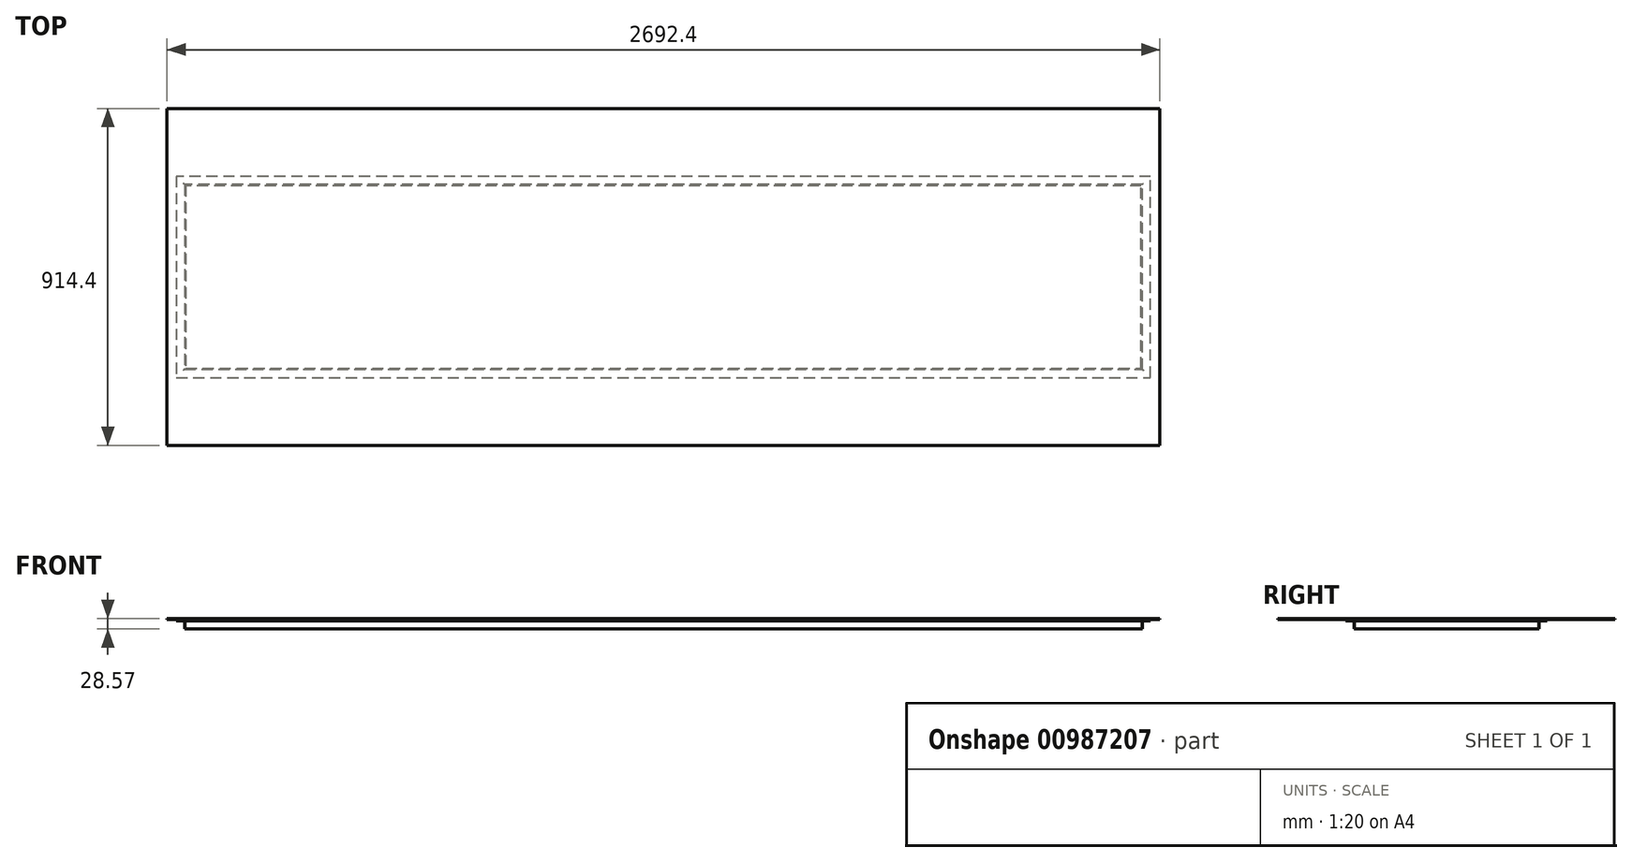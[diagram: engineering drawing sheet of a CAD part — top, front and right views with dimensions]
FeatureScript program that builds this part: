
annotation { "Feature Type Name" : "Feature", "Feature Type Description" : "" }
export const myFeature = defineFeature(function(context is Context, id is Id, definition is map)
    precondition{}
    {
        {
            var Q0;
            Q0=qCreatedBy(makeId("Top.planeOp"),FACE);
            var sketch = newSketch(context, id + "F0", { "sketchPlane" : qUnion([Q0])});
            skLineSegment(sketch, "E0.bottom", {"start": v(-1346.2, 457.2) * mm, "end": v(1346.2, 457.2) * mm});
            skLineSegment(sketch, "E0.top", {"start": v(-1346.2, -457.2) * mm, "end": v(1346.2, -457.2) * mm});
            skLineSegment(sketch, "E0.left", {"start": v(-1346.2, 457.2) * mm, "end": v(-1346.2, -457.2) * mm});
            skLineSegment(sketch, "E0.right", {"start": v(1346.2, 457.2) * mm, "end": v(1346.2, -457.2) * mm});
            skSolve(sketch);
        }
        {
            var Q0;
            Q0=makeQuery(id+"F0.imprint","IMPRINT",FACE,{"disambiguationData":[TD([[makeQuery(id+"F0.imprint","IMPRINT",EDGE,{"derivedFrom":sQuery(id+"F0.wireOp",EDGE,"E0.bottom")}),-1.0]])]});
            extrude(context, id + "F1", {"entities" : qUnion([Q0]), "depth" : 3.17 * mm, "offsetDistance" : 25.4 * mm});
        }
        {
            var Q0;
            Q0=makeQuery(id+"F1.opExtrude","CAP_FACE",FACE,{"disambiguationData":[OSD([sQuery(id+"F0.wireOp",EDGE,"E0.bottom"),sQuery(id+"F0.wireOp",EDGE,"E0.top"),sQuery(id+"F0.wireOp",EDGE,"E0.left"),sQuery(id+"F0.wireOp",EDGE,"E0.right")])],"isStart":true});
            var sketch = newSketch(context, id + "F2", { "sketchPlane" : qUnion([Q0])});
            skLineSegment(sketch, "E1.0", {"start": v(1295.4, 247.65) * mm, "end": v(-1295.4, 247.65) * mm});
            skLineSegment(sketch, "E2.0", {"start": v(-1295.4, 247.65) * mm, "end": v(-1295.4, -247.65) * mm});
            skLineSegment(sketch, "E3.0", {"start": v(-1295.4, -247.65) * mm, "end": v(1295.4, -247.65) * mm});
            skLineSegment(sketch, "E4.0", {"start": v(1295.4, -247.65) * mm, "end": v(1295.4, 247.65) * mm});
            skSolve(sketch);
        }
        {
            var Q0;
            Q0=qCreatedBy(makeId("Front.planeOp"),FACE);
            var sketch = newSketch(context, id + "F3", { "sketchPlane" : qUnion([Q0])});
            skPoint(sketch, "E5.0", {"position": v(-1295.4, 0) * mm});
            skLineSegment(sketch, "E6", {"start": v(-1295.4, 0) * mm, "end": v(-1320.8, 0) * mm});
            skLineSegment(sketch, "E7", {"start": v(-1320.8, 0) * mm, "end": v(-1320.8, -3.18) * mm});
            skLineSegment(sketch, "E8", {"start": v(-1320.8, -3.18) * mm, "end": v(-1301.75, -3.17) * mm});
            skLineSegment(sketch, "E9", {"start": v(-1298.58, -6.35) * mm, "end": v(-1298.58, -25.4) * mm});
            skLineSegment(sketch, "E10", {"start": v(-1298.58, -25.4) * mm, "end": v(-1295.4, -25.4) * mm});
            skLineSegment(sketch, "E11", {"start": v(-1295.4, -25.4) * mm, "end": v(-1295.4, 0) * mm});
            skPoint(sketch, "E12.visualSharp", {"position": v(-1298.58, -3.17) * mm});
            skArc(sketch, "E12.filletArc", {"start": v(-1298.58, -6.35) * mm, "mid": v(-1299.5, -4.1) * mm, "end": v(-1301.75, -3.18) * mm});
            skSolve(sketch);
        }
        {
            var Q0;
            Q0=makeQuery(id+"F3.imprint","IMPRINT",FACE,{"disambiguationData":[TD([[makeQuery(id+"F3.imprint","IMPRINT",EDGE,{"derivedFrom":sQuery(id+"F3.wireOp",EDGE,"E6")}),1.0]])]});
            var Q1;
            Q1=sQuery(id+"F2.wireOp",EDGE,"E2.0");
            var Q2;
            Q2=sQuery(id+"F2.wireOp",EDGE,"E1.0");
            var Q3;
            Q3=sQuery(id+"F2.wireOp",EDGE,"E4.0");
            var Q4;
            Q4=sQuery(id+"F2.wireOp",EDGE,"E3.0");
            sweep(context, id + "F4", {"operationType" : NewBodyOperationType.ADD, "profiles" : qUnion([Q0]), "path" : qUnion([Q1, Q2, Q3, Q4])});
        }
    });
